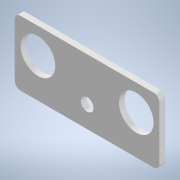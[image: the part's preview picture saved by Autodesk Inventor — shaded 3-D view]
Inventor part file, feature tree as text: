
AUTODESK INVENTOR PART (.ipt)
format: ipt  version: 2022.3 (Build 263350000, 350)  size: 160,768 bytes
history: native  units: mm
features: extrude x3, sketch x3, other x3, projected_geometry x2, fillet x1, reference x1
ambient origin geometry x8: Origin, YZ Plane, XZ Plane, XY Plane, X Axis, Y Axis, Z Axis, Center Point
bodies: Solid1 (feature_tree)
feature tree (13):
  extrude  "Extrusion1"  Depth=25.0mm
  extrude  "Extrusion2"  Depth=1.0mm
  extrude  "Extrusion3"  Depth=1.0mm
  fillet  "Fillet1"  Radius=6.0mm
  sketch  "Sketch1"  dims[d0=25.0mm d1=25.0mm]
  sketch  "Sketch3"  dims[d2=1.0mm d3=1.0mm]
  projected_geometry  "Projected Loop2"
  reference  "Reference1"
  sketch  "Sketch4"  dims[d4=1.0mm d5=1.0mm d6=6.0mm d7=6.0mm d8=10.0mm d9=1.3mm d10=2.0mm d11=1.0mm d12=0.0mm d13=1.0mm d14=0.0mm d15=1.0mm d16=0.0mm d17=1.0mm]
  projected_geometry  "Projected Loop3"
  other  "<userpath>\Documents\Inventor\NanoSumo\NanoSumo_part1.iam"
  other  "NanoSumo_part1.iam"
  other  "srodek:1"
